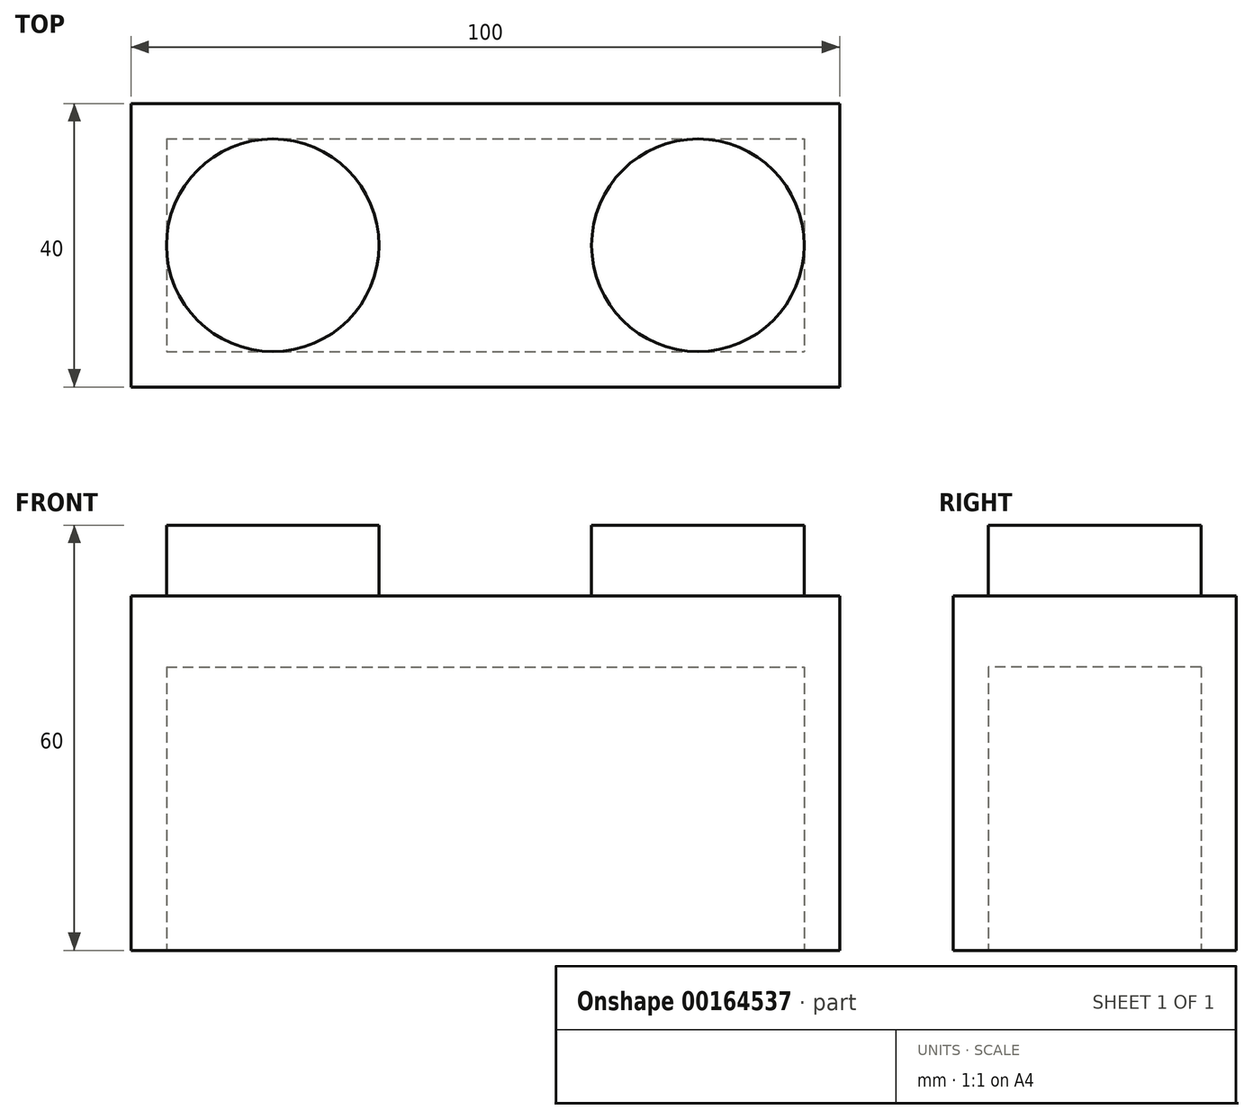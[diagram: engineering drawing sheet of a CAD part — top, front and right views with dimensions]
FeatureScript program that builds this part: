
annotation { "Feature Type Name" : "Feature", "Feature Type Description" : "" }
export const myFeature = defineFeature(function(context is Context, id is Id, definition is map)
    precondition{}
    {
        {
            var Q0;
            Q0=qCreatedBy(makeId("Front.planeOp"),FACE);
            var sketch = newSketch(context, id + "F0", { "sketchPlane" : qUnion([Q0])});
            skLineSegment(sketch, "E0.bottom", {"start": v(-50, -25) * mm, "end": v(50, -25) * mm});
            skLineSegment(sketch, "E0.top", {"start": v(-50, 25) * mm, "end": v(50, 25) * mm});
            skLineSegment(sketch, "E0.left", {"start": v(-50, -25) * mm, "end": v(-50, 25) * mm});
            skLineSegment(sketch, "E0.right", {"start": v(50, -25) * mm, "end": v(50, 25) * mm});
            skPoint(sketch, "E0.middle", {"position": v(0, 0) * mm});
            skSolve(sketch);
        }
        {
            var Q0;
            Q0 = qSketchRegion(id + "F0", true);
            extrude(context, id + "F1", {"entities" : qUnion([Q0]), "depth" : 40 * mm});
        }
        {
            var Q0;
            Q0=makeQuery(id+"F1.opExtrude","SWEPT_FACE",FACE,{"disambiguationData":[OSD([sQuery(id+"F0.wireOp",EDGE,"E0.top")])]});
            var sketch = newSketch(context, id + "F2", { "sketchPlane" : qUnion([Q0])});
            skCircle(sketch, "E1", {"center": v(-30, -20) * mm, "radius": 15 * mm});
            skPoint(sketch, "E1.centerSnap0", {"position": v(-50, -20) * mm});
            skCircle(sketch, "E2", {"center": v(30, -20) * mm, "radius": 15 * mm});
            skPoint(sketch, "E2.centerSnap0", {"position": v(50, -20) * mm});
            skSolve(sketch);
        }
        {
            var Q0;
            Q0 = qSketchRegion(id + "F2", true);
            extrude(context, id + "F3", {"entities" : qUnion([Q0]), "operationType" : NewBodyOperationType.ADD, "depth" : 10 * mm});
        }
        {
            var Q0;
            Q0=makeQuery(id+"F1.opExtrude","SWEPT_FACE",FACE,{"disambiguationData":[OSD([sQuery(id+"F0.wireOp",EDGE,"E0.bottom")])]});
            var sketch = newSketch(context, id + "F4", { "sketchPlane" : qUnion([Q0])});
            skLineSegment(sketch, "E3.bottom", {"start": v(-45, 5) * mm, "end": v(45, 5) * mm});
            skLineSegment(sketch, "E3.top", {"start": v(-45, 35) * mm, "end": v(45, 35) * mm});
            skLineSegment(sketch, "E3.left", {"start": v(-45, 5) * mm, "end": v(-45, 35) * mm});
            skLineSegment(sketch, "E3.right", {"start": v(45, 5) * mm, "end": v(45, 35) * mm});
            skPoint(sketch, "E3.middle", {"position": v(0, 20) * mm});
            skPoint(sketch, "E3.middle.positionSnap0", {"position": v(-50, 20) * mm});
            skPoint(sketch, "E3.centerSnap0", {"position": v(-50, 20) * mm});
            skSolve(sketch);
        }
        {
            var Q0;
            Q0 = qSketchRegion(id + "F4", true);
            extrude(context, id + "F5", {"entities" : qUnion([Q0]), "operationType" : NewBodyOperationType.REMOVE, "oppositeDirection" : true, "depth" : 40 * mm});
        }
    });
